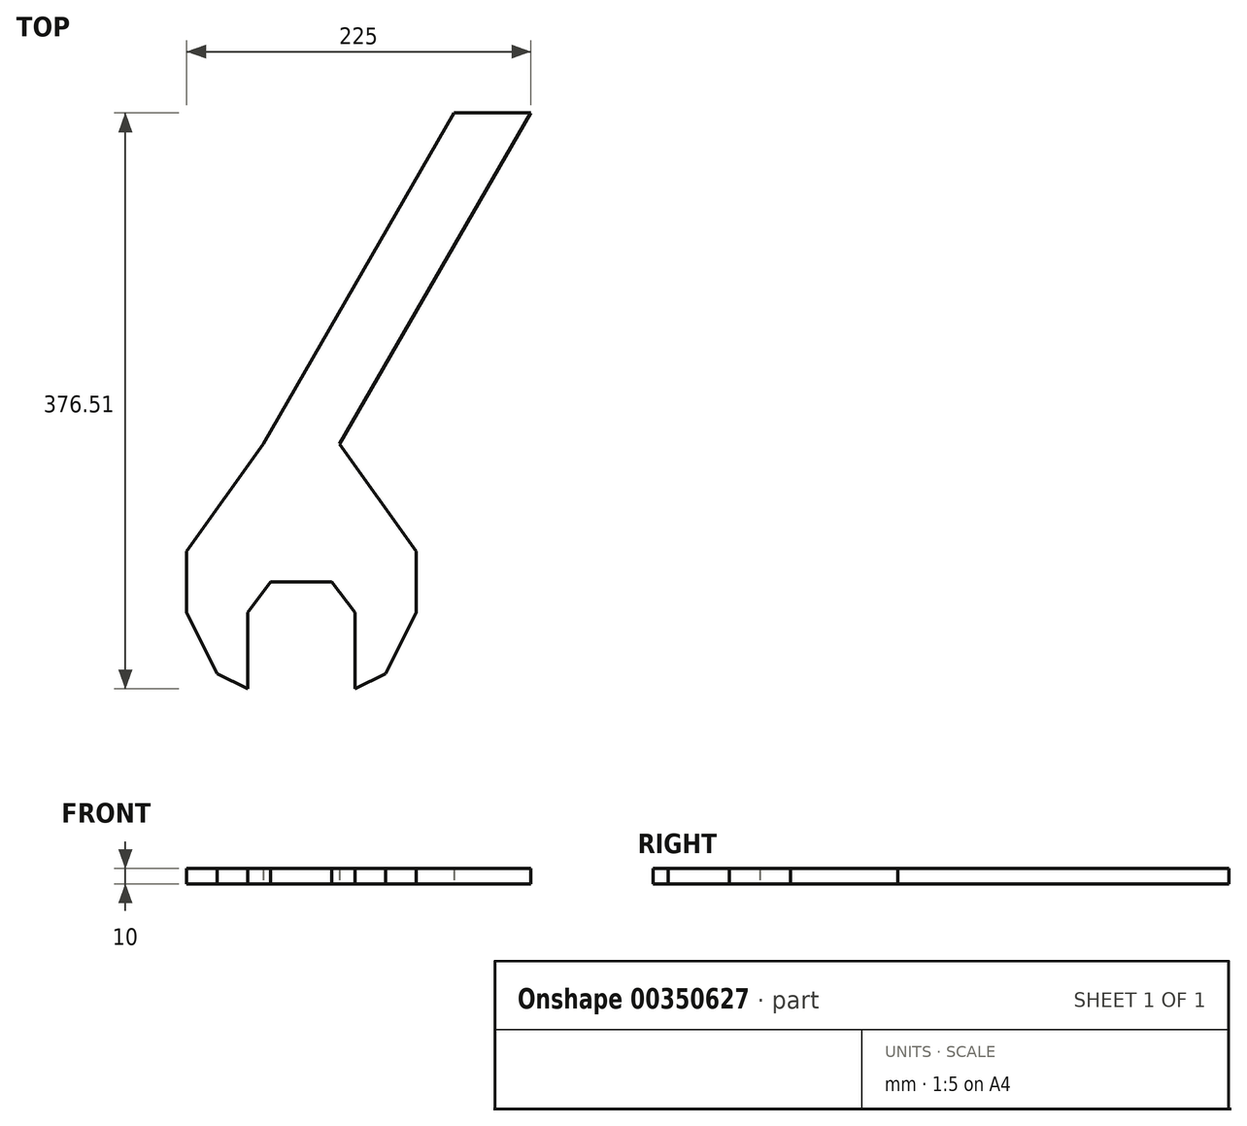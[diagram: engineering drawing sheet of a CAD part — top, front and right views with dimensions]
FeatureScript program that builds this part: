
annotation { "Feature Type Name" : "Feature", "Feature Type Description" : "" }
export const myFeature = defineFeature(function(context is Context, id is Id, definition is map)
    precondition{}
    {
        {
            var Q0;
            Q0=qCreatedBy(makeId("Top.planeOp"),FACE);
            var sketch = newSketch(context, id + "F0", { "sketchPlane" : qUnion([Q0])});
            skLineSegment(sketch, "E0", {"start": v(-20, 0) * mm, "end": v(20, 0) * mm});
            skLineSegment(sketch, "E1", {"start": v(-20, 0) * mm, "end": v(-35, -20) * mm});
            skLineSegment(sketch, "E2", {"start": v(-35, -20) * mm, "end": v(-35, -70) * mm});
            skLineSegment(sketch, "E3", {"start": v(0, 0) * mm, "end": v(0, -67.64) * mm, "construction": true});
            skLineSegment(sketch, "E4.MirrorCS", {"start": v(20, 0) * mm, "end": v(35, -20) * mm});
            skLineSegment(sketch, "E5.MirrorCS", {"start": v(35, -20) * mm, "end": v(35, -70) * mm});
            skLineSegment(sketch, "E6", {"start": v(-35, -70) * mm, "end": v(-55, -60) * mm});
            skLineSegment(sketch, "E7", {"start": v(-55, -60) * mm, "end": v(-75, -20) * mm});
            skLineSegment(sketch, "E8", {"start": v(-75, -20) * mm, "end": v(-75, 20) * mm});
            skLineSegment(sketch, "E9", {"start": v(-75, 20) * mm, "end": v(-25, 90) * mm});
            skLineSegment(sketch, "E10.MirrorCS", {"start": v(35, -70) * mm, "end": v(55, -60) * mm});
            skLineSegment(sketch, "E11.MirrorCS", {"start": v(55, -60) * mm, "end": v(75, -20) * mm});
            skLineSegment(sketch, "E12.MirrorCS", {"start": v(75, 20) * mm, "end": v(25, 90) * mm});
            skLineSegment(sketch, "E13.MirrorCS", {"start": v(75, -20) * mm, "end": v(75, 20) * mm});
            skLineSegment(sketch, "E14", {"start": v(-25, 90) * mm, "end": v(100, 306.5) * mm});
            skLineSegment(sketch, "E15", {"start": v(100, 306.5) * mm, "end": v(150, 306.5) * mm});
            skLineSegment(sketch, "E16", {"start": v(150, 306.5) * mm, "end": v(25, 90) * mm});
            skLineSegment(sketch, "E17", {"start": v(25, 90) * mm, "end": v(157.59, 90) * mm, "construction": true});
            skSolve(sketch);
        }
        {
            var Q0;
            Q0=makeQuery(id+"F0.imprint","IMPRINT",FACE,{"disambiguationData":[TD([[makeQuery(id+"F0.imprint","IMPRINT",EDGE,{"derivedFrom":sQuery(id+"F0.wireOp",EDGE,"E0")}),1.0]])]});
            extrude(context, id + "F1", {"entities" : qUnion([Q0]), "depth" : 10 * mm});
        }
    });
